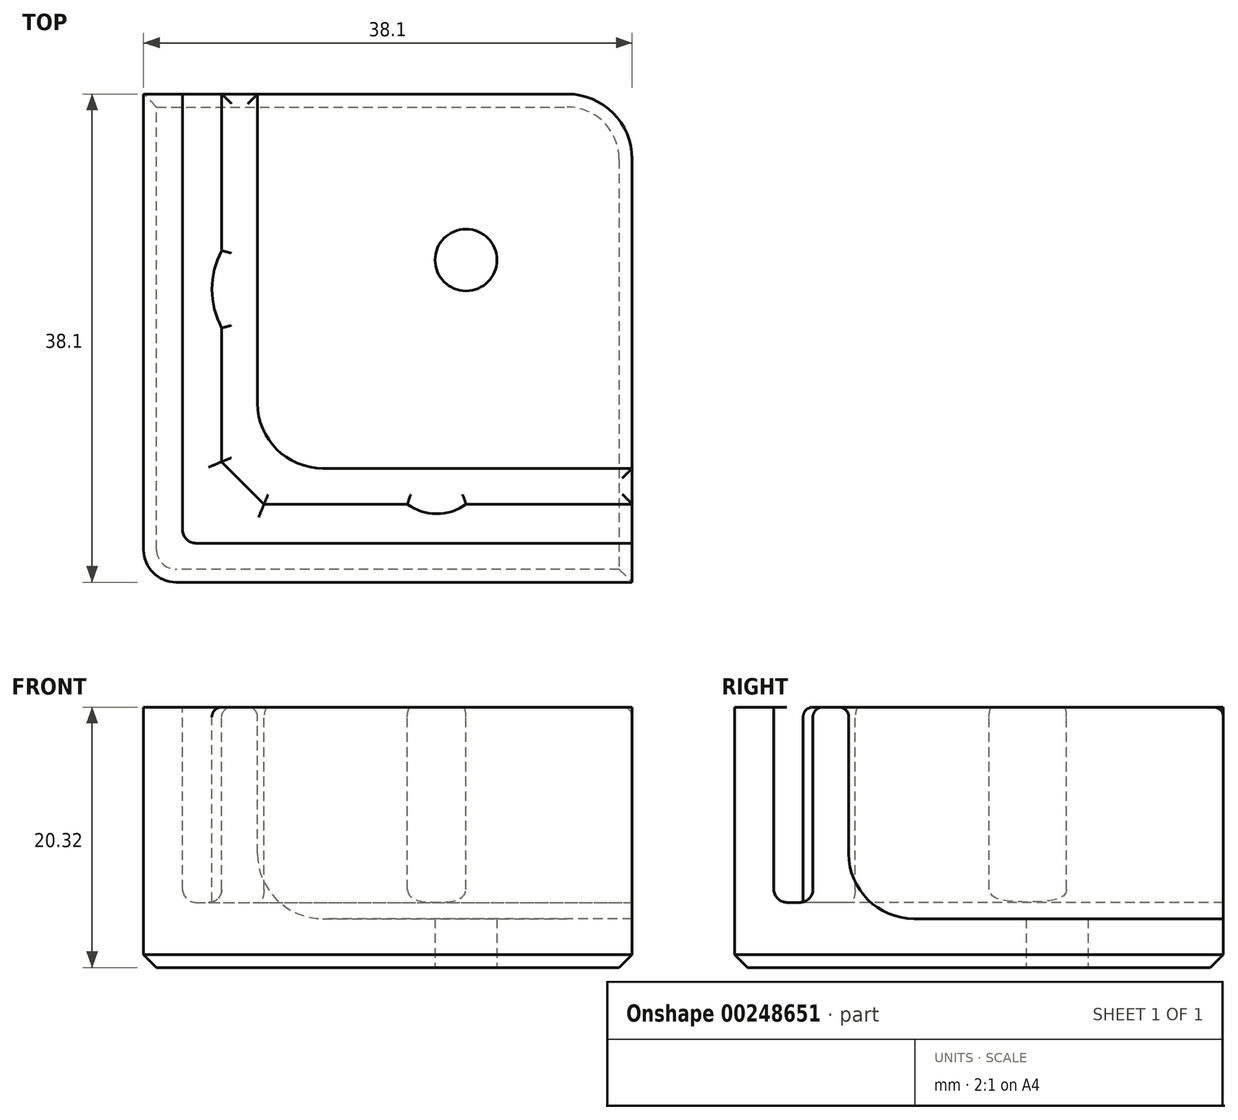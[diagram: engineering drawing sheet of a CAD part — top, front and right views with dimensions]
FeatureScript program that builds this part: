
annotation { "Feature Type Name" : "Feature", "Feature Type Description" : "" }
export const myFeature = defineFeature(function(context is Context, id is Id, definition is map)
    precondition{}
    {
        {
            var Q0;
            Q0=qCreatedBy(makeId("Top.planeOp"),FACE);
            var sketch = newSketch(context, id + "F0", { "sketchPlane" : qUnion([Q0])});
            skLineSegment(sketch, "E0.bottom", {"start": v(0, 0) * mm, "end": v(38.1, 0) * mm});
            skLineSegment(sketch, "E0.top", {"start": v(0, 38.1) * mm, "end": v(38.1, 38.1) * mm});
            skLineSegment(sketch, "E0.left", {"start": v(0, 0) * mm, "end": v(0, 38.1) * mm});
            skLineSegment(sketch, "E0.right", {"start": v(38.1, 0) * mm, "end": v(38.1, 38.1) * mm});
            skSolve(sketch);
        }
        {
            var Q0;
            Q0 = qSketchRegion(id + "F0", true);
            extrude(context, id + "F1", {"entities" : qUnion([Q0]), "depth" : 20.32 * mm});
        }
        {
            var Q0;
            Q0=makeQuery(id+"F1.opExtrude","CAP_FACE",FACE,{"disambiguationData":[OSD([sQuery(id+"F0.wireOp",EDGE,"E0.bottom"),sQuery(id+"F0.wireOp",EDGE,"E0.top"),sQuery(id+"F0.wireOp",EDGE,"E0.left"),sQuery(id+"F0.wireOp",EDGE,"E0.right")])],"isStart":false});
            var sketch = newSketch(context, id + "F2", { "sketchPlane" : qUnion([Q0])});
            skLineSegment(sketch, "E1.bottom", {"start": v(38.1, 38.1) * mm, "end": v(8.89, 38.1) * mm});
            skLineSegment(sketch, "E1.top", {"start": v(38.1, 8.9) * mm, "end": v(8.9, 8.89) * mm});
            skLineSegment(sketch, "E1.left", {"start": v(38.1, 38.1) * mm, "end": v(38.1, 8.9) * mm});
            skLineSegment(sketch, "E1.right", {"start": v(8.89, 38.1) * mm, "end": v(8.9, 8.89) * mm});
            skSolve(sketch);
        }
        {
            var Q0;
            Q0 = qSketchRegion(id + "F2", true);
            extrude(context, id + "F3", {"entities" : qUnion([Q0]), "operationType" : NewBodyOperationType.REMOVE, "oppositeDirection" : true, "depth" : 16.5 * mm});
        }
        {
            var Q0;
            Q0=makeQuery(id+"F1.opExtrude","CAP_FACE",FACE,{"disambiguationData":[OSD([sQuery(id+"F0.wireOp",EDGE,"E0.bottom"),sQuery(id+"F0.wireOp",EDGE,"E0.top"),sQuery(id+"F0.wireOp",EDGE,"E0.left"),sQuery(id+"F0.wireOp",EDGE,"E0.right")])],"isStart":false});
            var sketch = newSketch(context, id + "F4", { "sketchPlane" : qUnion([Q0])});
            skLineSegment(sketch, "E2", {"start": v(3.05, 38.1) * mm, "end": v(3.05, 3.05) * mm});
            skLineSegment(sketch, "E3", {"start": v(3.05, 3.05) * mm, "end": v(38.1, 3.05) * mm});
            skLineSegment(sketch, "E4.0", {"start": v(6.1, 6.1) * mm, "end": v(38.1, 6.1) * mm});
            skLineSegment(sketch, "E4.1", {"start": v(6.1, 38.1) * mm, "end": v(6.1, 6.1) * mm});
            skLineSegment(sketch, "E5", {"start": v(6.1, 9.4) * mm, "end": v(9.4, 6.1) * mm});
            skLineSegment(sketch, "E6.0", {"start": v(0, 38.1) * mm, "end": v(8.89, 38.1) * mm});
            skLineSegment(sketch, "E7.0", {"start": v(38.1, 0) * mm, "end": v(38.1, 8.9) * mm});
            skSolve(sketch);
        }
        {
            var Q0;
            Q0 = qSketchRegion(id + "F4", true);
            extrude(context, id + "F5", {"entities" : qUnion([Q0]), "operationType" : NewBodyOperationType.REMOVE, "oppositeDirection" : true, "depth" : 15.24 * mm});
        }
        {
            var Q0;
            Q0=makeQuery(id+"F1.opExtrude","SWEPT_EDGE",EDGE,{"disambiguationData":[OSD([sQuery(id+"F0.wireOp",EDGE,"E0.top"),sQuery(id+"F0.wireOp",EDGE,"E0.right")])]});
            fillet(context, id + "F6", {"entities" : qUnion([Q0]), "radius" : 5.08 * mm, "tangentPropagation" : true, "allowEdgeOverflow" : false});
        }
        {
            var Q0;
            Q0=makeQuery(id+"F3.boolean.opBoolean","COPY",EDGE,{"derivedFrom":makeQuery(id+"F3.opExtrude","SWEPT_EDGE",EDGE,{"disambiguationData":[OSD([sQuery(id+"F2.wireOp",EDGE,"E1.top"),sQuery(id+"F2.wireOp",EDGE,"E1.right")])]})});
            fillet(context, id + "F7", {"entities" : qUnion([Q0]), "radius" : 5.08 * mm, "tangentPropagation" : true, "allowEdgeOverflow" : false});
        }
        {
            var Q0;
            Q0=makeQuery(id+"F3.boolean.opBoolean","COPY",EDGE,{"derivedFrom":makeQuery(id+"F3.opExtrude","CAP_EDGE",EDGE,{"disambiguationData":[OSD([sQuery(id+"F2.wireOp",EDGE,"E1.top")])],"isStart":false})});
            var Q1;
            {var subQ0=sQuery(id+"F2.wireOp",EDGE,"E1.right");var subQ1=sQuery(id+"F2.wireOp",EDGE,"E1.top");Q1=makeQuery(id+"F7.opFillet","BLEND_EDGE",EDGE,{"blendedFrom":[makeQuery(id+"F3.boolean.opBoolean","COPY",EDGE,{"derivedFrom":makeQuery(id+"F3.opExtrude","SWEPT_EDGE",EDGE,{"disambiguationData":[OSD([subQ1,subQ0])]})}),makeQuery(id+"F3.boolean.opBoolean","COPY",FACE,{"derivedFrom":makeQuery(id+"F3.opExtrude","CAP_FACE",FACE,{"disambiguationData":[OSD([sQuery(id+"F2.wireOp",EDGE,"E1.bottom"),subQ1,sQuery(id+"F2.wireOp",EDGE,"E1.left"),subQ0])],"isStart":false})})],"blendedInto":[makeQuery(id+"F3.boolean.opBoolean","COPY",FACE,{"derivedFrom":makeQuery(id+"F3.opExtrude","CAP_FACE",FACE,{"disambiguationData":[OSD([sQuery(id+"F2.wireOp",EDGE,"E1.bottom"),subQ1,sQuery(id+"F2.wireOp",EDGE,"E1.left"),subQ0])],"isStart":false})})]});}
            var Q2;
            Q2=makeQuery(id+"F3.boolean.opBoolean","COPY",EDGE,{"derivedFrom":makeQuery(id+"F3.opExtrude","CAP_EDGE",EDGE,{"disambiguationData":[OSD([sQuery(id+"F2.wireOp",EDGE,"E1.right")])],"isStart":false})});
            fillet(context, id + "F8", {"entities" : qUnion([Q0, Q1, Q2]), "radius" : 5.08 * mm, "tangentPropagation" : true, "allowEdgeOverflow" : false});
        }
        {
            var Q0;
            Q0=makeQuery(id+"F1.opExtrude","SWEPT_EDGE",EDGE,{"disambiguationData":[OSD([sQuery(id+"F0.wireOp",EDGE,"E0.bottom"),sQuery(id+"F0.wireOp",EDGE,"E0.left")])]});
            fillet(context, id + "F9", {"entities" : qUnion([Q0]), "radius" : 2.54 * mm, "tangentPropagation" : true, "allowEdgeOverflow" : false});
        }
        {
            var Q0;
            Q0=makeQuery(id+"F1.opExtrude","CAP_FACE",FACE,{"disambiguationData":[OSD([sQuery(id+"F0.wireOp",EDGE,"E0.bottom"),sQuery(id+"F0.wireOp",EDGE,"E0.top"),sQuery(id+"F0.wireOp",EDGE,"E0.left"),sQuery(id+"F0.wireOp",EDGE,"E0.right")])],"isStart":true});
            var sketch = newSketch(context, id + "F10", { "sketchPlane" : qUnion([Q0])});
            skLineSegment(sketch, "E8", {"start": v(0, 0) * mm, "end": v(37.35, -37.35) * mm, "construction": true});
            skCircle(sketch, "E9", {"center": v(25.14, -25.14) * mm, "radius": 2.41 * mm});
            skSolve(sketch);
        }
        {
            var Q0;
            Q0 = qSketchRegion(id + "F10", true);
            extrude(context, id + "F11", {"entities" : qUnion([Q0]), "operationType" : NewBodyOperationType.REMOVE, "endBound" : BoundingType.THROUGH_ALL, "oppositeDirection" : true, "depth" : 25.4 * mm});
        }
        {
            var Q0;
            {var subQ0=sQuery(id+"F0.wireOp",EDGE,"E0.top");var subQ1=sQuery(id+"F0.wireOp",EDGE,"E0.right");Q0=makeQuery(id+"F5.boolean.opBoolean","SPLIT",FACE,{"disambiguationData":[TD([makeQuery(id+"F3.boolean.opBoolean","COPY",FACE,{"derivedFrom":makeQuery(id+"F3.opExtrude","SWEPT_FACE",FACE,{"disambiguationData":[OSD([sQuery(id+"F2.wireOp",EDGE,"E1.top")])]})})])],"derivedFrom":makeQuery(id+"F1.opExtrude","CAP_FACE",FACE,{"disambiguationData":[OSD([sQuery(id+"F0.wireOp",EDGE,"E0.bottom"),subQ0,sQuery(id+"F0.wireOp",EDGE,"E0.left"),subQ1])],"isStart":false})});}
            var sketch = newSketch(context, id + "F12", { "sketchPlane" : qUnion([Q0])});
            skArc(sketch, "E10", {"start": v(20.57, 6.1) * mm, "mid": v(22.86, 5.33) * mm, "end": v(25.15, 6.1) * mm});
            skLineSegment(sketch, "E11", {"start": v(20.57, 6.1) * mm, "end": v(25.15, 6.1) * mm});
            skArc(sketch, "E12", {"start": v(6.1, 25.88) * mm, "mid": v(5.33, 22.86) * mm, "end": v(6.1, 19.84) * mm});
            skLineSegment(sketch, "E13", {"start": v(6.1, 25.88) * mm, "end": v(6.1, 19.84) * mm});
            skSolve(sketch);
        }
        {
            var Q0;
            Q0 = qSketchRegion(id + "F12", true);
            extrude(context, id + "F13", {"entities" : qUnion([Q0]), "operationType" : NewBodyOperationType.ADD, "endBound" : BoundingType.UP_TO_NEXT, "oppositeDirection" : true, "depth" : 25.4 * mm});
        }
        {
            var Q0;
            Q0=makeQuery(id+"F5.boolean.opBoolean","COPY",EDGE,{"derivedFrom":makeQuery(id+"F5.opExtrude","SWEPT_EDGE",EDGE,{"disambiguationData":[OSD([sQuery(id+"F4.wireOp",EDGE,"E2"),sQuery(id+"F4.wireOp",EDGE,"E3")])]})});
            var Q1;
            Q1=makeQuery(id+"F5.boolean.opBoolean","COPY",EDGE,{"derivedFrom":makeQuery(id+"F5.opExtrude","CAP_EDGE",EDGE,{"disambiguationData":[OSD([sQuery(id+"F4.wireOp",EDGE,"E3")])],"isStart":false})});
            var Q2;
            Q2=makeQuery(id+"F5.boolean.opBoolean","COPY",EDGE,{"derivedFrom":makeQuery(id+"F5.opExtrude","CAP_EDGE",EDGE,{"disambiguationData":[OSD([sQuery(id+"F4.wireOp",EDGE,"E2")])],"isStart":false})});
            var Q3;
            {var subQ0=sQuery(id+"F4.wireOp",EDGE,"E4.0");Q3=makeQuery(id+"F13.boolean.opBoolean","SPLIT",EDGE,{"disambiguationData":[TD([makeQuery(id+"F1.opExtrude","SWEPT_FACE",FACE,{"disambiguationData":[OSD([sQuery(id+"F0.wireOp",EDGE,"E0.right")])]})])],"derivedFrom":makeQuery(id+"F5.boolean.opBoolean","COPY",EDGE,{"derivedFrom":makeQuery(id+"F5.opExtrude","CAP_EDGE",EDGE,{"disambiguationData":[OSD([subQ0])],"isStart":false})})});}
            var Q4;
            Q4=makeQuery(id+"F5.boolean.opBoolean","COPY",EDGE,{"derivedFrom":makeQuery(id+"F5.opExtrude","CAP_EDGE",EDGE,{"disambiguationData":[OSD([sQuery(id+"F4.wireOp",EDGE,"E5")])],"isStart":false})});
            var Q5;
            {var subQ0=sQuery(id+"F4.wireOp",EDGE,"E5");var subQ1=sQuery(id+"F4.wireOp",EDGE,"E4.1");Q5=makeQuery(id+"F13.boolean.opBoolean","SPLIT",EDGE,{"disambiguationData":[TD([makeQuery(id+"F5.boolean.opBoolean","COPY",FACE,{"derivedFrom":makeQuery(id+"F5.opExtrude","SWEPT_FACE",FACE,{"disambiguationData":[OSD([subQ0])]})})])],"derivedFrom":makeQuery(id+"F5.boolean.opBoolean","COPY",EDGE,{"derivedFrom":makeQuery(id+"F5.opExtrude","CAP_EDGE",EDGE,{"disambiguationData":[OSD([subQ1])],"isStart":false})})});}
            var Q6;
            {var subQ0=sQuery(id+"F4.wireOp",EDGE,"E4.1");Q6=makeQuery(id+"F13.boolean.opBoolean","SPLIT",EDGE,{"disambiguationData":[TD([makeQuery(id+"F1.opExtrude","SWEPT_FACE",FACE,{"disambiguationData":[OSD([sQuery(id+"F0.wireOp",EDGE,"E0.top")])]})])],"derivedFrom":makeQuery(id+"F5.boolean.opBoolean","COPY",EDGE,{"derivedFrom":makeQuery(id+"F5.opExtrude","CAP_EDGE",EDGE,{"disambiguationData":[OSD([subQ0])],"isStart":false})})});}
            var Q7;
            {var subQ0=sQuery(id+"F4.wireOp",EDGE,"E5");var subQ1=sQuery(id+"F4.wireOp",EDGE,"E4.0");Q7=makeQuery(id+"F13.boolean.opBoolean","SPLIT",EDGE,{"disambiguationData":[TD([makeQuery(id+"F5.boolean.opBoolean","COPY",FACE,{"derivedFrom":makeQuery(id+"F5.opExtrude","SWEPT_FACE",FACE,{"disambiguationData":[OSD([subQ0])]})})])],"derivedFrom":makeQuery(id+"F5.boolean.opBoolean","COPY",EDGE,{"derivedFrom":makeQuery(id+"F5.opExtrude","CAP_EDGE",EDGE,{"disambiguationData":[OSD([subQ1])],"isStart":false})})});}
            var Q8;
            Q8=makeQuery(id+"F13.opExtrude","CAP_EDGE",EDGE,{"disambiguationData":[OSD([sQuery(id+"F12.wireOp",EDGE,"E10")])],"isStart":false});
            fillet(context, id + "F14", {"entities" : qUnion([Q0, Q1, Q2, Q3, Q4, Q5, Q6, Q7, Q8]), "radius" : 1.02 * mm, "tangentPropagation" : true, "allowEdgeOverflow" : false});
        }
        {
            var Q0;
            Q0=makeQuery(id+"F1.opExtrude","CAP_EDGE",EDGE,{"disambiguationData":[OSD([sQuery(id+"F0.wireOp",EDGE,"E0.bottom")])],"isStart":true});
            var Q1;
            Q1=makeQuery(id+"F1.opExtrude","CAP_EDGE",EDGE,{"disambiguationData":[OSD([sQuery(id+"F0.wireOp",EDGE,"E0.top")])],"isStart":true});
            var Q2;
            {var subQ0=sQuery(id+"F0.wireOp",EDGE,"E0.right");var subQ1=sQuery(id+"F0.wireOp",EDGE,"E0.top");Q2=makeQuery(id+"F6.opFillet","BLEND_EDGE",EDGE,{"blendedFrom":[makeQuery(id+"F1.opExtrude","SWEPT_EDGE",EDGE,{"disambiguationData":[OSD([subQ1,subQ0])]}),makeQuery(id+"F1.opExtrude","CAP_FACE",FACE,{"disambiguationData":[OSD([sQuery(id+"F0.wireOp",EDGE,"E0.bottom"),subQ1,sQuery(id+"F0.wireOp",EDGE,"E0.left"),subQ0])],"isStart":true})],"blendedInto":[makeQuery(id+"F1.opExtrude","CAP_FACE",FACE,{"disambiguationData":[OSD([sQuery(id+"F0.wireOp",EDGE,"E0.bottom"),subQ1,sQuery(id+"F0.wireOp",EDGE,"E0.left"),subQ0])],"isStart":true})]});}
            chamfer(context, id + "F15", {"entities" : qUnion([Q0, Q1, Q2]), "width" : 1.02 * mm, "tangentPropagation" : true});
        }
        {
            var Q0;
            Q0=makeQuery(id+"F5.boolean.opBoolean","COPY",EDGE,{"derivedFrom":makeQuery(id+"F5.opExtrude","CAP_EDGE",EDGE,{"disambiguationData":[OSD([sQuery(id+"F4.wireOp",EDGE,"E2")])],"isStart":true})});
            var Q1;
            {var subQ1=sQuery(id+"F4.wireOp",EDGE,"E4.0");var subQ2=sQuery(id+"F0.wireOp",EDGE,"E0.right");Q1=makeQuery(id+"F13.boolean.opBoolean","SPLIT",EDGE,{"disambiguationData":[TD([makeQuery(id+"F1.opExtrude","SWEPT_FACE",FACE,{"disambiguationData":[OSD([subQ2])]})])],"derivedFrom":makeQuery(id+"F5.boolean.opBoolean","COPY",EDGE,{"derivedFrom":makeQuery(id+"F5.opExtrude","CAP_EDGE",EDGE,{"disambiguationData":[OSD([subQ1])],"isStart":true})})});}
            var Q2;
            Q2=makeQuery(id+"F13.opExtrude","CAP_EDGE",EDGE,{"disambiguationData":[OSD([sQuery(id+"F12.wireOp",EDGE,"E10")])],"isStart":true});
            var Q3;
            {var subQ0=sQuery(id+"F0.wireOp",EDGE,"E0.right");var subQ1=sQuery(id+"F0.wireOp",EDGE,"E0.top");Q3=makeQuery(id+"F13.boolean.opBoolean","MERGE",FACE,{"derivedFrom":[makeQuery(id+"F5.boolean.opBoolean","SPLIT",FACE,{"disambiguationData":[TD([makeQuery(id+"F3.boolean.opBoolean","COPY",FACE,{"derivedFrom":makeQuery(id+"F3.opExtrude","SWEPT_FACE",FACE,{"disambiguationData":[OSD([sQuery(id+"F2.wireOp",EDGE,"E1.top")])]})})])],"derivedFrom":makeQuery(id+"F1.opExtrude","CAP_FACE",FACE,{"disambiguationData":[OSD([sQuery(id+"F0.wireOp",EDGE,"E0.bottom"),subQ1,sQuery(id+"F0.wireOp",EDGE,"E0.left"),subQ0])],"isStart":false})}),makeQuery(id+"F13.opExtrude","CAP_FACE",FACE,{"disambiguationData":[OSD([sQuery(id+"F12.wireOp",EDGE,"E10"),sQuery(id+"F12.wireOp",EDGE,"E11")])],"isStart":true}),makeQuery(id+"F13.opExtrude","CAP_FACE",FACE,{"disambiguationData":[OSD([sQuery(id+"F12.wireOp",EDGE,"E12"),sQuery(id+"F12.wireOp",EDGE,"E13")])],"isStart":true})]});}
            fillet(context, id + "F16", {"entities" : qUnion([Q0, Q1, Q2, Q3]), "radius" : 0.76 * mm, "tangentPropagation" : true, "allowEdgeOverflow" : false});
        }
    });
